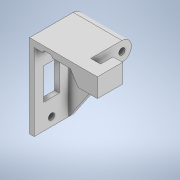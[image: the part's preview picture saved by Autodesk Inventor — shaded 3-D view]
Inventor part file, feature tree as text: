
AUTODESK INVENTOR PART (.ipt)
format: ipt  version: 2022 (Build 260153000, 153)  size: 241,664 bytes
history: native  units: in
note: dims shown in document units (in); Inventor stores cm internally (conversion verified against a paired STEP export)
features: extrude x12, sketch x12, chamfer x1
ambient origin geometry x8: Origin, YZ Plane, XZ Plane, XY Plane, X Axis, Y Axis, Z Axis, Center Point
bodies: Solid1 (feature_tree)
feature tree (25):
  extrude  "Extrusion1"  Depth=0.122in
  extrude  "Extrusion2"  Depth=0.1181in
  extrude  "Extrusion3"  Depth=0.2362in TaperAngle=0.0deg
  extrude  "Extrusion4"  Depth=0.0787in
  extrude  "Extrusion5"  Depth=0.315in
  extrude  "Extrusion6"  Depth=0.3937in
  extrude  "Extrusion7"  Depth=0.5512in
  extrude  "Extrusion8"  Depth=0.1575in
  extrude  "Extrusion9"  Depth=0.1575in
  extrude  "Extrusion10"  Depth=0.3937in TaperAngle=0.0deg
  chamfer  "Chamfer1"  Distance=0.3937in
  extrude  "Extrusion11"  Depth=1.0433in TaperAngle=0.0deg
  extrude  "Extrusion12"  Depth=0.1181in
  sketch  "Sketch1"  dims[d1=0.6693in d2=0.122in]
  sketch  "Sketch2"  dims[d3=0.1181in d4=0.1181in]
  sketch  "Sketch3"  dims[d5=0.2441in d6=0.2362in d7=0.0in]
  sketch  "Sketch4"  dims[d8=0.122in d9=0.0787in]
  sketch  "Sketch5"  dims[d10=0.2362in d11=0.0in d13=0.315in]
  sketch  "Sketch7"  dims[d14=0.3937in d15=0.0in d17=0.5118in]
  sketch  "Sketch8"  dims[d18=0.4921in d19=0.5512in]
  sketch  "Sketch9"  dims[d20=0.1575in d21=0.0in d22=0.0984in]
  sketch  "Sketch11"  dims[d23=0.1575in d24=0.0in d25=0.4528in]
  sketch  "Sketch13"  dims[d26=0.4331in d27=0.3937in d28=0.0in d29=0.3937in d30=0.0in]
  sketch  "Sketch14"  dims[d31=0.4331in d32=1.0433in d33=0.0in]
  sketch  "Sketch15"  dims[d34=0.0787in d35=0.0in d36=0.1083in d37=0.1083in d38=0.0787in d39=0.0787in d40=0.3937in d41=0.1969in d42=0.1181in d43=0.2165in d44=0.2165in d45=0.0787in d46=0.0in d47=0.0984in d48=0.1575in d49=45.0deg d50=0.0197in d51=0.0in d52=0.0591in d53=0.0591in d54=0.0591in d56=0.0in d57=0.1181in d58=0.0in]
